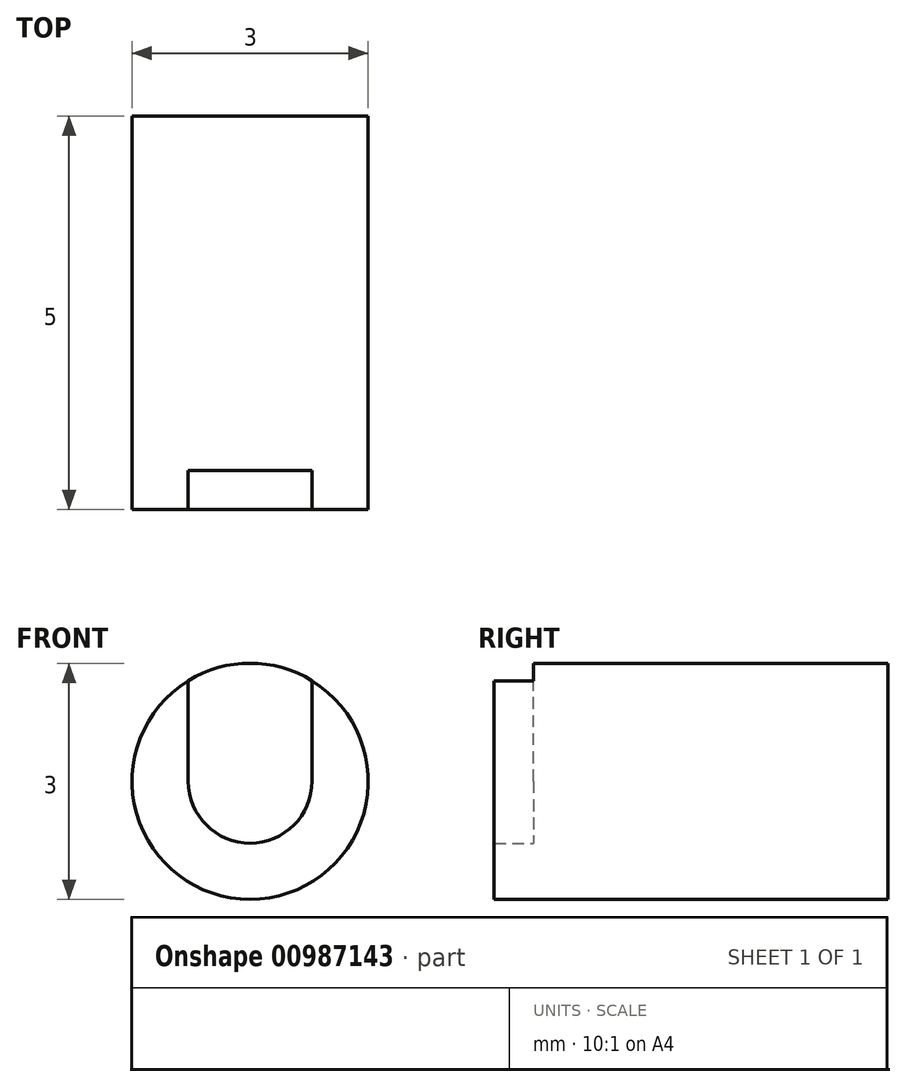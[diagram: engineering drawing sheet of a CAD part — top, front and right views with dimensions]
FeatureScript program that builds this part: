
annotation { "Feature Type Name" : "Feature", "Feature Type Description" : "" }
export const myFeature = defineFeature(function(context is Context, id is Id, definition is map)
    precondition{}
    {
        {
            var Q0;
            Q0=qCreatedBy(makeId("Front.planeOp"),FACE);
            var sketch = newSketch(context, id + "F0", { "sketchPlane" : qUnion([Q0])});
            skCircle(sketch, "E0", {"center": v(0, 0) * mm, "radius": 1.5 * mm});
            skLineSegment(sketch, "E1", {"start": v(-0.79, 1.28) * mm, "end": v(-0.79, 0) * mm});
            skLineSegment(sketch, "E2", {"start": v(0.79, 1.28) * mm, "end": v(0.79, 0) * mm});
            skCircle(sketch, "E3", {"center": v(0, 0) * mm, "radius": 0.79 * mm});
            skSolve(sketch);
        }
        {
            var Q0;
            {var subQ0=sQuery(id+"F0.wireOp",EDGE,"E1");Q0=makeQuery(id+"F0.imprint","IMPRINT",FACE,{"disambiguationData":[TD([[makeQuery(id+"F0.imprint","IMPRINT",EDGE,{"derivedFrom":subQ0}),-1.0]])]});}
            extrude(context, id + "F1", {"entities" : qUnion([Q0]), "depth" : 5 * mm, "offsetDistance" : 25 * mm});
        }
        {
            var Q0;
            Q0=makeQuery(id+"F1.opExtrude","CAP_FACE",FACE,{"disambiguationData":[OSD([sQuery(id+"F0.wireOp",EDGE,"E0"),sQuery(id+"F0.wireOp",EDGE,"E1"),sQuery(id+"F0.wireOp",EDGE,"E2"),sQuery(id+"F0.wireOp",EDGE,"E3")])],"isStart":true});
            var sketch = newSketch(context, id + "F2", { "sketchPlane" : qUnion([Q0])});
            skCircle(sketch, "E4", {"center": v(0, 0) * mm, "radius": 1.5 * mm});
            skSolve(sketch);
        }
        {
            var Q0;
            Q0 = qSketchRegion(id + "F2", true);
            extrude(context, id + "F3", {"entities" : qUnion([Q0]), "operationType" : NewBodyOperationType.ADD, "oppositeDirection" : true, "depth" : 4.5 * mm, "offsetDistance" : 25 * mm});
        }
    });
